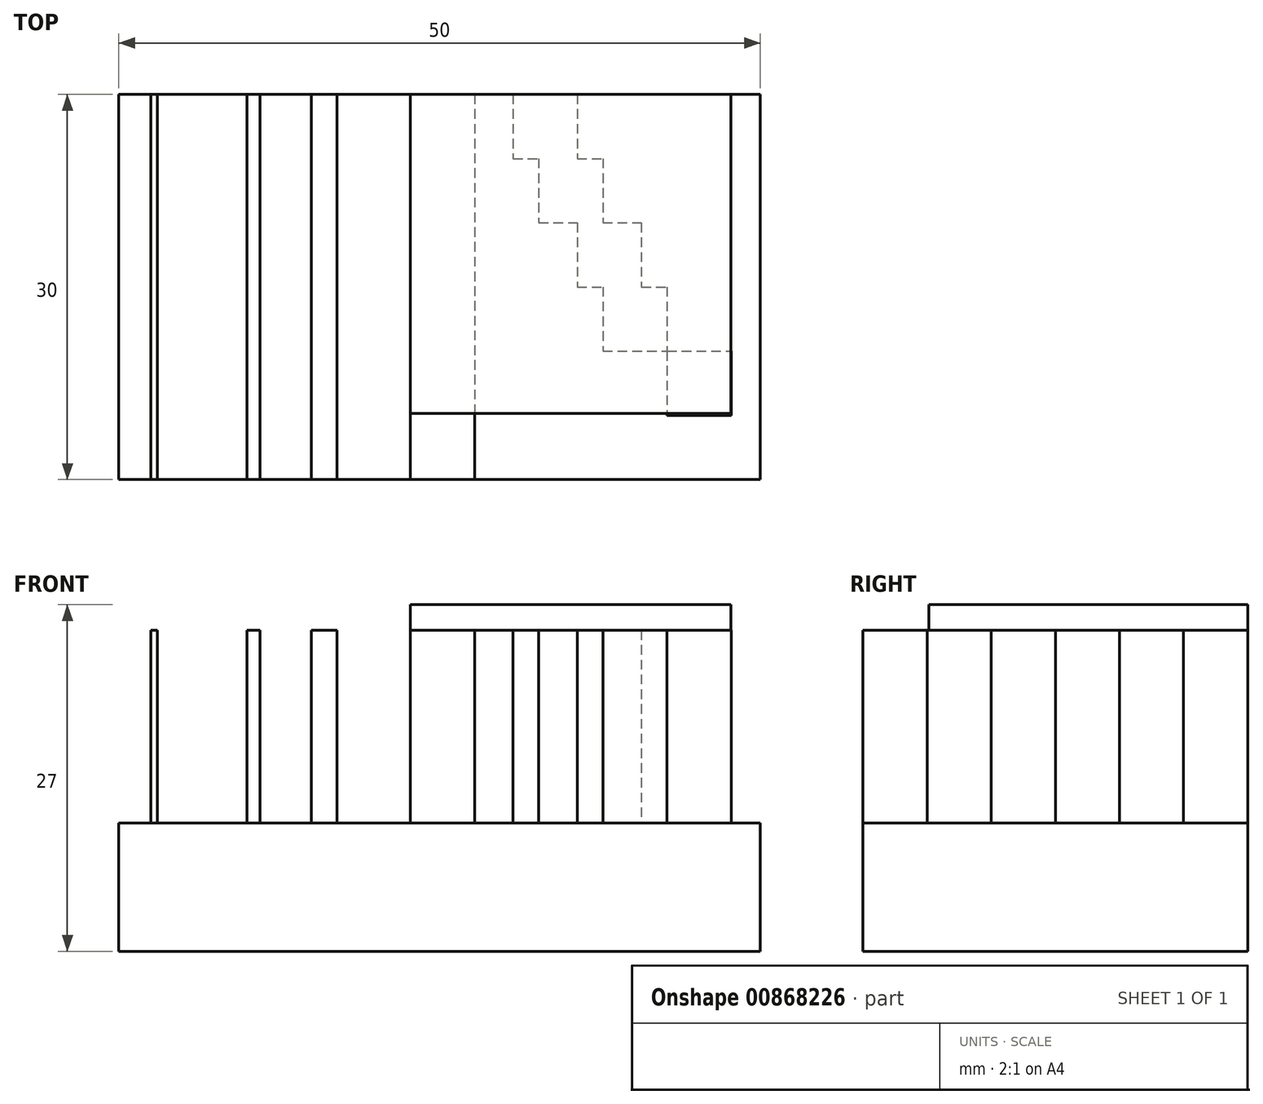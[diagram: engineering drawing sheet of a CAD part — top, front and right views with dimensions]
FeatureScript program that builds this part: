
annotation { "Feature Type Name" : "Feature", "Feature Type Description" : "" }
export const myFeature = defineFeature(function(context is Context, id is Id, definition is map)
    precondition{}
    {
        {
            var Q0;
            Q0=qCreatedBy(makeId("Top.planeOp"),FACE);
            var sketch = newSketch(context, id + "F0", { "sketchPlane" : qUnion([Q0])});
            skLineSegment(sketch, "E0.bottom", {"start": v(0, 30) * mm, "end": v(50, 30) * mm});
            skLineSegment(sketch, "E0.top", {"start": v(0, 0) * mm, "end": v(50, 0) * mm});
            skLineSegment(sketch, "E0.left", {"start": v(0, 30) * mm, "end": v(0, 0) * mm});
            skLineSegment(sketch, "E0.right", {"start": v(50, 30) * mm, "end": v(50, 0) * mm});
            skSolve(sketch);
        }
        {
            var Q0;
            Q0 = qSketchRegion(id + "F0", true);
            extrude(context, id + "F1", {"entities" : qUnion([Q0]), "depth" : 10 * mm, "offsetDistance" : 25 * mm});
        }
        {
            var Q0;
            Q0=makeQuery(id+"F1.opExtrude","CAP_FACE",FACE,{"disambiguationData":[OSD([sQuery(id+"F0.wireOp",EDGE,"E0.bottom"),sQuery(id+"F0.wireOp",EDGE,"E0.top"),sQuery(id+"F0.wireOp",EDGE,"E0.left"),sQuery(id+"F0.wireOp",EDGE,"E0.right")])],"isStart":false});
            var sketch = newSketch(context, id + "F2", { "sketchPlane" : qUnion([Q0])});
            skLineSegment(sketch, "E1.0", {"start": v(0, 30) * mm, "end": v(0, 0) * mm, "construction": true});
            skLineSegment(sketch, "E2.bottom", {"start": v(2.5, 0) * mm, "end": v(3, 0) * mm});
            skLineSegment(sketch, "E2.top", {"start": v(2.5, 30) * mm, "end": v(3, 30) * mm});
            skLineSegment(sketch, "E2.left", {"start": v(2.5, 0) * mm, "end": v(2.5, 30) * mm});
            skLineSegment(sketch, "E2.right", {"start": v(3, 0) * mm, "end": v(3, 30) * mm});
            skLineSegment(sketch, "E3.bottom", {"start": v(10, 0) * mm, "end": v(11, 0) * mm});
            skLineSegment(sketch, "E3.top", {"start": v(10, 30) * mm, "end": v(11, 30) * mm});
            skLineSegment(sketch, "E3.left", {"start": v(10, 0) * mm, "end": v(10, 30) * mm});
            skLineSegment(sketch, "E3.right", {"start": v(11, 0) * mm, "end": v(11, 30) * mm});
            skLineSegment(sketch, "E4.bottom", {"start": v(15, 30) * mm, "end": v(17, 30) * mm});
            skLineSegment(sketch, "E4.top", {"start": v(15, 0) * mm, "end": v(17, 0) * mm});
            skLineSegment(sketch, "E4.left", {"start": v(15, 30) * mm, "end": v(15, 0) * mm});
            skLineSegment(sketch, "E4.right", {"start": v(17, 30) * mm, "end": v(17, 0) * mm});
            skLineSegment(sketch, "E5.bottom", {"start": v(22.73, 30) * mm, "end": v(27.73, 30) * mm});
            skLineSegment(sketch, "E5.top", {"start": v(22.73, 0) * mm, "end": v(27.73, 0) * mm});
            skLineSegment(sketch, "E5.left", {"start": v(22.73, 30) * mm, "end": v(22.73, 0) * mm});
            skLineSegment(sketch, "E5.right", {"start": v(27.73, 30) * mm, "end": v(27.73, 0) * mm});
            skLineSegment(sketch, "E6.bottom", {"start": v(30.73, 30) * mm, "end": v(35.73, 30) * mm});
            skLineSegment(sketch, "E6.top", {"start": v(30.73, 25) * mm, "end": v(35.73, 25) * mm});
            skLineSegment(sketch, "E6.left", {"start": v(30.73, 30) * mm, "end": v(30.73, 25) * mm});
            skLineSegment(sketch, "E6.right", {"start": v(35.73, 30) * mm, "end": v(35.73, 25) * mm});
            skLineSegment(sketch, "E7.bottom", {"start": v(32.73, 25) * mm, "end": v(37.73, 25) * mm});
            skLineSegment(sketch, "E7.top", {"start": v(32.73, 20) * mm, "end": v(37.73, 20) * mm});
            skLineSegment(sketch, "E7.left", {"start": v(32.73, 25) * mm, "end": v(32.73, 20) * mm});
            skLineSegment(sketch, "E7.right", {"start": v(37.73, 25) * mm, "end": v(37.73, 20) * mm});
            skLineSegment(sketch, "E8.bottom", {"start": v(35.73, 20) * mm, "end": v(40.73, 20) * mm});
            skLineSegment(sketch, "E8.top", {"start": v(35.73, 15) * mm, "end": v(40.73, 15) * mm});
            skLineSegment(sketch, "E8.left", {"start": v(35.73, 20) * mm, "end": v(35.73, 15) * mm});
            skLineSegment(sketch, "E8.right", {"start": v(40.73, 20) * mm, "end": v(40.73, 15) * mm});
            skLineSegment(sketch, "E9.bottom", {"start": v(37.73, 15) * mm, "end": v(42.73, 15) * mm});
            skLineSegment(sketch, "E9.top", {"start": v(37.73, 10) * mm, "end": v(42.73, 10) * mm});
            skLineSegment(sketch, "E9.left", {"start": v(37.73, 15) * mm, "end": v(37.73, 10) * mm});
            skLineSegment(sketch, "E9.right", {"start": v(42.73, 15) * mm, "end": v(42.73, 10) * mm});
            skLineSegment(sketch, "E10.bottom", {"start": v(42.73, 10) * mm, "end": v(47.73, 10) * mm});
            skLineSegment(sketch, "E10.top", {"start": v(42.73, 5) * mm, "end": v(47.73, 5) * mm});
            skLineSegment(sketch, "E10.left", {"start": v(42.73, 10) * mm, "end": v(42.73, 5) * mm});
            skLineSegment(sketch, "E10.right", {"start": v(47.73, 10) * mm, "end": v(47.73, 5) * mm});
            skSolve(sketch);
        }
        {
            var Q0;
            Q0 = qSketchRegion(id + "F2", true);
            extrude(context, id + "F3", {"entities" : qUnion([Q0]), "depth" : 15 * mm, "offsetDistance" : 25 * mm});
        }
        {
            var Q0;
            Q0=makeQuery(id+"F3.opExtrude","CAP_FACE",FACE,{"disambiguationData":[OSD([sQuery(id+"F2.wireOp",EDGE,"E5.bottom"),sQuery(id+"F2.wireOp",EDGE,"E5.top"),sQuery(id+"F2.wireOp",EDGE,"E5.left"),sQuery(id+"F2.wireOp",EDGE,"E5.right")])],"isStart":false});
            var sketch = newSketch(context, id + "F4", { "sketchPlane" : qUnion([Q0])});
            skLineSegment(sketch, "E11.bottom", {"start": v(22.73, 30) * mm, "end": v(47.71, 30) * mm});
            skLineSegment(sketch, "E11.top", {"start": v(22.73, 5.15) * mm, "end": v(47.71, 5.15) * mm});
            skLineSegment(sketch, "E11.left", {"start": v(22.73, 30) * mm, "end": v(22.73, 5.15) * mm});
            skLineSegment(sketch, "E11.right", {"start": v(47.71, 30) * mm, "end": v(47.71, 5.15) * mm});
            skSolve(sketch);
        }
        {
            var Q0;
            Q0 = qSketchRegion(id + "F4", true);
            extrude(context, id + "F5", {"entities" : qUnion([Q0]), "depth" : 2 * mm, "offsetDistance" : 25 * mm});
        }
    });
